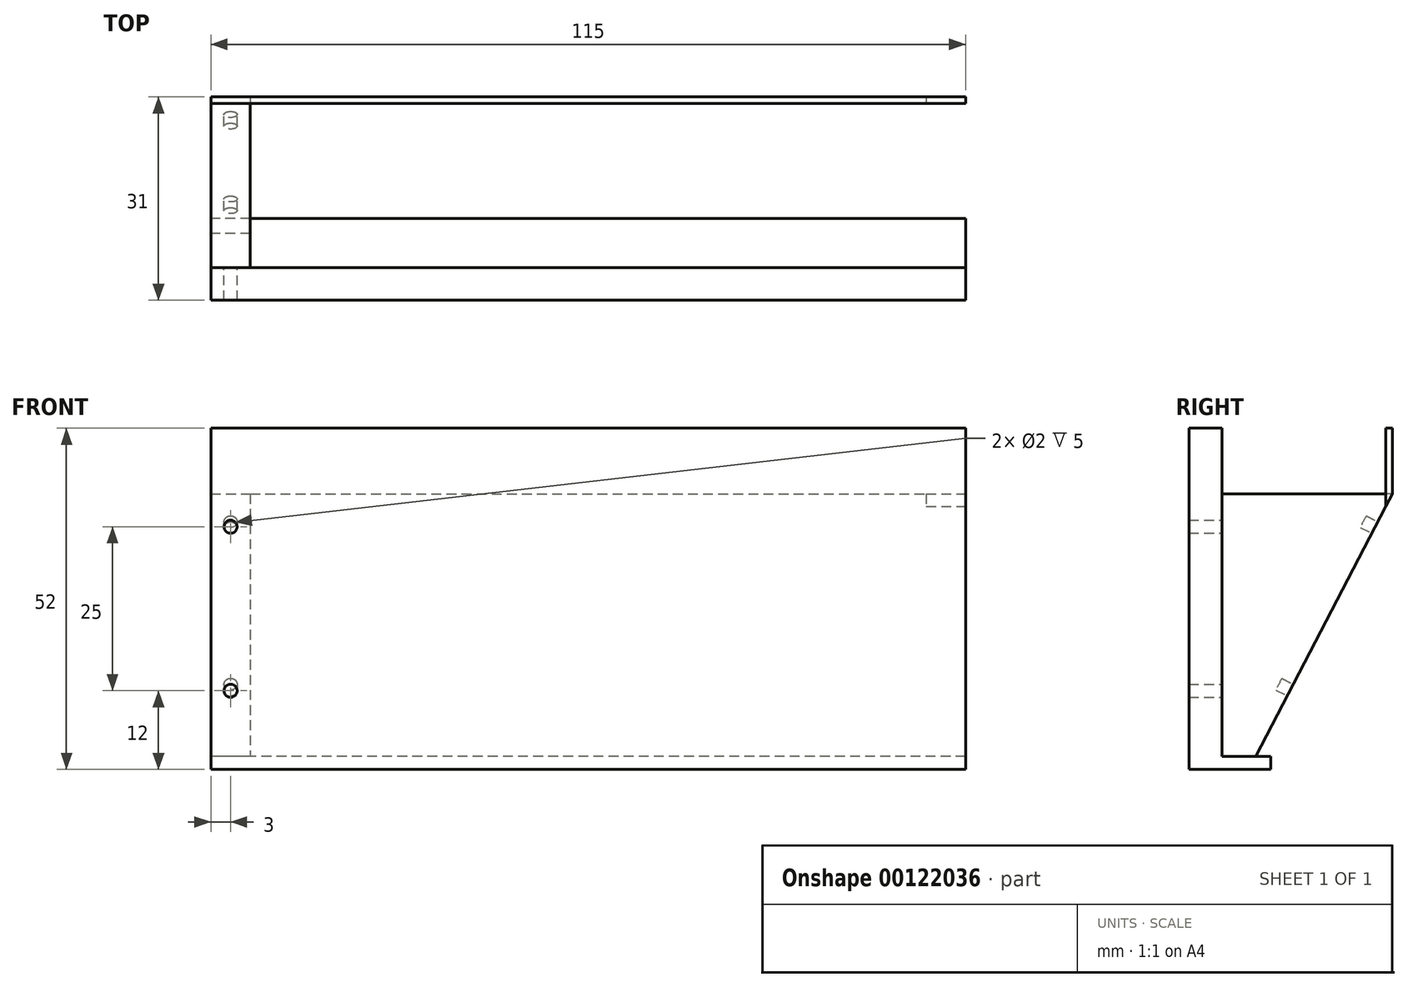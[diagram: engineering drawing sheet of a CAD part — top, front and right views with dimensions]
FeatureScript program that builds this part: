
annotation { "Feature Type Name" : "Feature", "Feature Type Description" : "" }
export const myFeature = defineFeature(function(context is Context, id is Id, definition is map)
    precondition{}
    {
        {
            var Q0;
            Q0=qCreatedBy(makeId("Top.planeOp"),FACE);
            var sketch = newSketch(context, id + "F0", { "sketchPlane" : qUnion([Q0])});
            skLineSegment(sketch, "E0.bottom", {"start": v(0, 0) * mm, "end": v(115, 0) * mm});
            skLineSegment(sketch, "E0.top", {"start": v(0, 26) * mm, "end": v(115, 26) * mm});
            skLineSegment(sketch, "E0.left", {"start": v(0, 0) * mm, "end": v(0, 26) * mm});
            skLineSegment(sketch, "E0.right", {"start": v(115, 0) * mm, "end": v(115, 26) * mm});
            skLineSegment(sketch, "E1", {"start": v(57.5, 26) * mm, "end": v(57.5, 13) * mm, "construction": true});
            skPoint(sketch, "E1.endSnap0", {"position": v(0, 13) * mm});
            skText(sketch, "E2", { "text": "MARTIN", "fontName": "AllertaStencil-Regular.ttf"});
            skPoint(sketch, "E3", {"position": v(57.5, 13) * mm});
            const initialGuessF0  = {"E2": [0.00395, 0.003, 1, 0, 0.02]};
            skSetInitialGuess(sketch, initialGuessF0);
            skSolve(sketch);
        }
        {
            var Q0;
            Q0=qCreatedBy(makeId("Front.planeOp"),FACE);
            var sketch = newSketch(context, id + "F1", { "sketchPlane" : qUnion([Q0])});
            skLineSegment(sketch, "E4.bottom", {"start": v(0, 0) * mm, "end": v(115, 0) * mm});
            skLineSegment(sketch, "E4.top", {"start": v(0, -60) * mm, "end": v(115, -60) * mm});
            skLineSegment(sketch, "E4.left", {"start": v(0, 0) * mm, "end": v(0, -60) * mm});
            skLineSegment(sketch, "E4.right", {"start": v(115, 0) * mm, "end": v(115, -60) * mm});
            skLineSegment(sketch, "E5", {"start": v(115, -60) * mm, "end": v(109, -60) * mm, "construction": true});
            skLineSegment(sketch, "E6", {"start": v(109, -60) * mm, "end": v(109, 0) * mm, "construction": true});
            skLineSegment(sketch, "E7", {"start": v(0, 0) * mm, "end": v(6, 0) * mm, "construction": true});
            skLineSegment(sketch, "E8", {"start": v(6, 0) * mm, "end": v(6, -60) * mm, "construction": true});
            skLineSegment(sketch, "E9", {"start": v(109, 0) * mm, "end": v(115, 0) * mm, "construction": true});
            skLineSegment(sketch, "E10", {"start": v(112, 0) * mm, "end": v(112, -60) * mm, "construction": true});
            skLineSegment(sketch, "E11", {"start": v(112, 0) * mm, "end": v(112, -15) * mm, "construction": true});
            skCircle(sketch, "E12", {"center": v(112, -15) * mm, "radius": 1 * mm});
            skLineSegment(sketch, "E13", {"start": v(112, -60) * mm, "end": v(112, -40) * mm, "construction": true});
            skCircle(sketch, "E14", {"center": v(112, -40) * mm, "radius": 1 * mm});
            skLineSegment(sketch, "E15", {"start": v(57.5, 0) * mm, "end": v(57.5, -60) * mm, "construction": true});
            skCircle(sketch, "E16.MirrorC", {"center": v(3, -15) * mm, "radius": 1 * mm});
            skLineSegment(sketch, "E17.MirrorCS", {"start": v(3, 0) * mm, "end": v(3, -60) * mm, "construction": true});
            skCircle(sketch, "E18.MirrorC", {"center": v(3, -40) * mm, "radius": 1 * mm});
            skLineSegment(sketch, "E19", {"start": v(0, -60) * mm, "end": v(0, -52) * mm, "construction": true});
            skPoint(sketch, "E20.endSnap0", {"position": v(112, -50) * mm});
            skLineSegment(sketch, "E21", {"start": v(0, -52) * mm, "end": v(115, -52) * mm});
            skSolve(sketch);
        }
        {
            var Q0;
            Q0=qCreatedBy(makeId("Right.planeOp"),FACE);
            var sketch = newSketch(context, id + "F2", { "sketchPlane" : qUnion([Q0])});
            skLineSegment(sketch, "E22.bottom", {"start": v(0, 0) * mm, "end": v(26, 0) * mm});
            skLineSegment(sketch, "E22.top", {"start": v(0, -60) * mm, "end": v(26, -60) * mm});
            skLineSegment(sketch, "E22.left", {"start": v(0, 0) * mm, "end": v(0, -60) * mm});
            skLineSegment(sketch, "E22.right", {"start": v(26, 0) * mm, "end": v(26, -60) * mm});
            skLineSegment(sketch, "E23", {"start": v(26, 0) * mm, "end": v(26, -10) * mm, "construction": true});
            skLineSegment(sketch, "E24", {"start": v(26, -10) * mm, "end": v(0, -60) * mm});
            skLineSegment(sketch, "E25", {"start": v(26, -10) * mm, "end": v(0, -10) * mm});
            skLineSegment(sketch, "E26", {"start": v(0, -60) * mm, "end": v(0, -50) * mm, "construction": true});
            skLineSegment(sketch, "E27.bottom", {"start": v(0, -50) * mm, "end": v(7.45, -50) * mm});
            skLineSegment(sketch, "E27.left", {"start": v(0, -50) * mm, "end": v(0, -52) * mm, "construction": true});
            skLineSegment(sketch, "E27.right", {"start": v(7.45, -50) * mm, "end": v(7.45, -52) * mm, "construction": true});
            skLineSegment(sketch, "E28", {"start": v(7.45, -52) * mm, "end": v(0, -52) * mm});
            skLineSegment(sketch, "E29", {"start": v(7.45, -52) * mm, "end": v(7.45, -50) * mm});
            skLineSegment(sketch, "E30", {"start": v(7.45, -50) * mm, "end": v(5.2, -50) * mm});
            skPoint(sketch, "E31", {"position": v(0, -52) * mm});
            skLineSegment(sketch, "E32", {"start": v(0, -52) * mm, "end": v(0, -40) * mm, "construction": true});
            skLineSegment(sketch, "E33", {"start": v(0, -40) * mm, "end": v(10.4, -40) * mm, "construction": true});
            skLineSegment(sketch, "E34", {"start": v(0, -40) * mm, "end": v(0, -15) * mm, "construction": true});
            skLineSegment(sketch, "E35", {"start": v(0, -15) * mm, "end": v(23.4, -15) * mm, "construction": true});
            skSolve(sketch);
        }
        {
            var Q0;
            Q0=makeQuery(id+"F2.imprint","IMPRINT",FACE,{"disambiguationData":[TD([[makeQuery(id+"F2.imprint","IMPRINT",EDGE,{"derivedFrom":sQuery(id+"F2.wireOp",EDGE,"E22.bottom")}),-1.0]])]});
            cPlane(context, id + "F3", {"entities" : qUnion([Q0]), "cplaneType" : CPlaneType.OFFSET, "offset" : 115 * mm, "width" : 150 * mm, "height" : 150 * mm});
        }
        {
            var Q0;
            Q0=qCreatedBy(id+"F3.planeOp",FACE);
            var sketch = newSketch(context, id + "F4", { "sketchPlane" : qUnion([Q0])});
            skLineSegment(sketch, "E36.bottom", {"start": v(0, 0) * mm, "end": v(26, 0) * mm});
            skLineSegment(sketch, "E36.top", {"start": v(0, -60) * mm, "end": v(26, -60) * mm});
            skLineSegment(sketch, "E36.left", {"start": v(0, 0) * mm, "end": v(0, -60) * mm});
            skLineSegment(sketch, "E36.right", {"start": v(26, 0) * mm, "end": v(26, -60) * mm});
            skLineSegment(sketch, "E37", {"start": v(26, 0) * mm, "end": v(26, -10) * mm, "construction": true});
            skLineSegment(sketch, "E38", {"start": v(26, -10) * mm, "end": v(0, -60) * mm});
            skLineSegment(sketch, "E39", {"start": v(26, -10) * mm, "end": v(0, -10) * mm});
            skSolve(sketch);
        }
        {
            var Q0;
            Q0=makeQuery(id+"F0.imprint","IMPRINT",FACE,{"disambiguationData":[TD([[makeQuery(id+"F0.imprint","IMPRINT",EDGE,{"derivedFrom":sQuery(id+"F0.wireOp",EDGE,"E0.bottom")}),1.0]])]});
            extrude(context, id + "F5", {"entities" : qUnion([Q0]), "oppositeDirection" : true, "depth" : 10 * mm});
        }
        {
            var Q0;
            {var subQ0=sQuery(id+"F2.wireOp",EDGE,"E24");Q0=makeQuery(id+"F2.imprint","IMPRINT",FACE,{"disambiguationData":[TD([[makeQuery(id+"F2.imprint","IMPRINT",EDGE,{"derivedFrom":subQ0}),-1.0]])]});}
            extrude(context, id + "F6", {"entities" : qUnion([Q0]), "operationType" : NewBodyOperationType.ADD, "depth" : 6 * mm});
        }
        {
            var Q0;
            {var subQ0=sQuery(id+"F4.wireOp",EDGE,"E38");Q0=makeQuery(id+"F4.imprint","IMPRINT",FACE,{"disambiguationData":[TD([[makeQuery(id+"F4.imprint","IMPRINT",EDGE,{"derivedFrom":subQ0}),-1.0]])]});}
            extrude(context, id + "F7", {"entities" : qUnion([Q0]), "operationType" : NewBodyOperationType.ADD, "oppositeDirection" : true, "depth" : 6 * mm});
        }
        {
            var Q0;
            Q0=makeQuery(id+"F1.imprint","IMPRINT",FACE,{"disambiguationData":[TD([[makeQuery(id+"F1.imprint","IMPRINT",EDGE,{"derivedFrom":sQuery(id+"F1.wireOp",EDGE,"E16.MirrorC")}),-1.0]])]});
            var Q1;
            Q1=makeQuery(id+"F1.imprint","IMPRINT",FACE,{"disambiguationData":[TD([[makeQuery(id+"F1.imprint","IMPRINT",EDGE,{"derivedFrom":sQuery(id+"F1.wireOp",EDGE,"E18.MirrorC")}),-1.0]])]});
            var Q2;
            Q2=makeQuery(id+"F1.imprint","IMPRINT",FACE,{"disambiguationData":[TD([[makeQuery(id+"F1.imprint","IMPRINT",EDGE,{"derivedFrom":sQuery(id+"F1.wireOp",EDGE,"E14")}),1.0]])]});
            var Q3;
            Q3=makeQuery(id+"F1.imprint","IMPRINT",FACE,{"disambiguationData":[TD([[makeQuery(id+"F1.imprint","IMPRINT",EDGE,{"derivedFrom":sQuery(id+"F1.wireOp",EDGE,"E12")}),1.0]])]});
            var Q4;
            Q4=sQuery(id+"F1.wireOp",EDGE,"E12");
            var Q5;
            Q5=sQuery(id+"F1.wireOp",EDGE,"E14");
            var Q6;
            Q6=sQuery(id+"F1.wireOp",EDGE,"E18.MirrorC");
            var Q7;
            Q7=sQuery(id+"F1.wireOp",EDGE,"E16.MirrorC");
            extrude(context, id + "F8", {"entities" : qUnion([Q0, Q1, Q2, Q3]), "operationType" : NewBodyOperationType.REMOVE, "surfaceEntities" : qUnion([Q4, Q5, Q6, Q7]), "oppositeDirection" : true, "depth" : 25 * mm});
        }
        {
            var Q0;
            Q0=makeQuery(id+"F1.imprint","IMPRINT",FACE,{"disambiguationData":[TD([[makeQuery(id+"F1.imprint","IMPRINT",EDGE,{"derivedFrom":sQuery(id+"F1.wireOp",EDGE,"E4.bottom")}),-1.0]])]});
            var Q1;
            Q1=makeQuery(id+"F1.imprint","IMPRINT",FACE,{"disambiguationData":[TD([[makeQuery(id+"F1.imprint","IMPRINT",EDGE,{"derivedFrom":sQuery(id+"F1.wireOp",EDGE,"E16.MirrorC")}),-1.0]])]});
            var Q2;
            Q2=makeQuery(id+"F1.imprint","IMPRINT",FACE,{"disambiguationData":[TD([[makeQuery(id+"F1.imprint","IMPRINT",EDGE,{"derivedFrom":sQuery(id+"F1.wireOp",EDGE,"E18.MirrorC")}),-1.0]])]});
            var Q3;
            Q3=makeQuery(id+"F1.imprint","IMPRINT",FACE,{"disambiguationData":[TD([[makeQuery(id+"F1.imprint","IMPRINT",EDGE,{"derivedFrom":sQuery(id+"F1.wireOp",EDGE,"E14")}),1.0]])]});
            var Q4;
            Q4=makeQuery(id+"F1.imprint","IMPRINT",FACE,{"disambiguationData":[TD([[makeQuery(id+"F1.imprint","IMPRINT",EDGE,{"derivedFrom":sQuery(id+"F1.wireOp",EDGE,"E12")}),1.0]])]});
            extrude(context, id + "F9", {"entities" : qUnion([Q0, Q1, Q2, Q3, Q4]), "operationType" : NewBodyOperationType.ADD, "depth" : 5 * mm});
        }
        {
            var Q0;
            {var subQ0=sQuery(id+"F2.wireOp",EDGE,"E25");Q0=makeQuery(id+"F2.imprint","IMPRINT",FACE,{"disambiguationData":[TD([[makeQuery(id+"F2.imprint","IMPRINT",EDGE,{"derivedFrom":subQ0}),1.0]])]});}
            extrude(context, id + "F10", {"entities" : qUnion([Q0]), "operationType" : NewBodyOperationType.ADD, "depth" : 6 * mm});
        }
        {
            var Q0;
            {var subQ0=sQuery(id+"F1.wireOp",EDGE,"E4.top");Q0=makeQuery(id+"F1.imprint","IMPRINT",FACE,{"disambiguationData":[TD([[makeQuery(id+"F1.imprint","IMPRINT",EDGE,{"derivedFrom":subQ0}),1.0]])]});}
            extrude(context, id + "F11", {"entities" : qUnion([Q0]), "operationType" : NewBodyOperationType.REMOVE, "oppositeDirection" : true, "depth" : 6 * mm});
        }
        {
            var Q0;
            {var subQ0=sQuery(id+"F1.wireOp",EDGE,"E4.top");Q0=makeQuery(id+"F1.imprint","IMPRINT",FACE,{"disambiguationData":[TD([[makeQuery(id+"F1.imprint","IMPRINT",EDGE,{"derivedFrom":subQ0}),1.0]])]});}
            var Q1;
            Q1=sQuery(id+"F1.wireOp",EDGE,"E18.MirrorC");
            extrude(context, id + "F12", {"entities" : qUnion([Q0]), "operationType" : NewBodyOperationType.REMOVE, "surfaceEntities" : qUnion([Q1]), "oppositeDirection" : true, "depth" : 25 * mm});
        }
        {
            var Q0;
            Q0=makeQuery(id+"F10.opExtrude","SWEPT_FACE",FACE,{"disambiguationData":[OSD([sQuery(id+"F2.wireOp",EDGE,"E24")])]});
            var sketch = newSketch(context, id + "F13", { "sketchPlane" : qUnion([Q0])});
            skLineSegment(sketch, "E40", {"start": v(0, -30.6) * mm, "end": v(-6, -30.6) * mm, "construction": true});
            skCircle(sketch, "E41", {"center": v(-3, -30.6) * mm, "radius": 1 * mm});
            skLineSegment(sketch, "E42", {"start": v(0, -2.69) * mm, "end": v(-6, -2.69) * mm, "construction": true});
            skCircle(sketch, "E43", {"center": v(-3, -2.69) * mm, "radius": 1 * mm});
            skSolve(sketch);
        }
        {
            var Q0;
            Q0=makeQuery(id+"F13.imprint","IMPRINT",FACE,{"disambiguationData":[TD([[makeQuery(id+"F13.imprint","IMPRINT",EDGE,{"derivedFrom":sQuery(id+"F13.wireOp",EDGE,"E41")}),1.0]])]});
            var Q1;
            Q1=makeQuery(id+"F13.imprint","IMPRINT",FACE,{"disambiguationData":[TD([[makeQuery(id+"F13.imprint","IMPRINT",EDGE,{"derivedFrom":sQuery(id+"F13.wireOp",EDGE,"E43")}),1.0]])]});
            extrude(context, id + "F14", {"entities" : qUnion([Q0, Q1]), "operationType" : NewBodyOperationType.REMOVE, "oppositeDirection" : true, "depth" : 2 * mm});
        }
        {
            var Q0;
            {var subQ0=sQuery(id+"F2.wireOp",EDGE,"E27.bottom");Q0=makeQuery(id+"F2.imprint","IMPRINT",FACE,{"disambiguationData":[TD([[makeQuery(id+"F2.imprint","IMPRINT",EDGE,{"derivedFrom":subQ0}),-1.0]])]});}
            var Q1;
            {var subQ4=sQuery(id+"F2.wireOp",EDGE,"E29");Q1=makeQuery(id+"F2.imprint","IMPRINT",FACE,{"disambiguationData":[TD([[makeQuery(id+"F2.imprint","IMPRINT",EDGE,{"derivedFrom":subQ4}),1.0]])]});}
            extrude(context, id + "F15", {"entities" : qUnion([Q0, Q1]), "operationType" : NewBodyOperationType.ADD, "depth" : 115 * mm});
        }
    });
